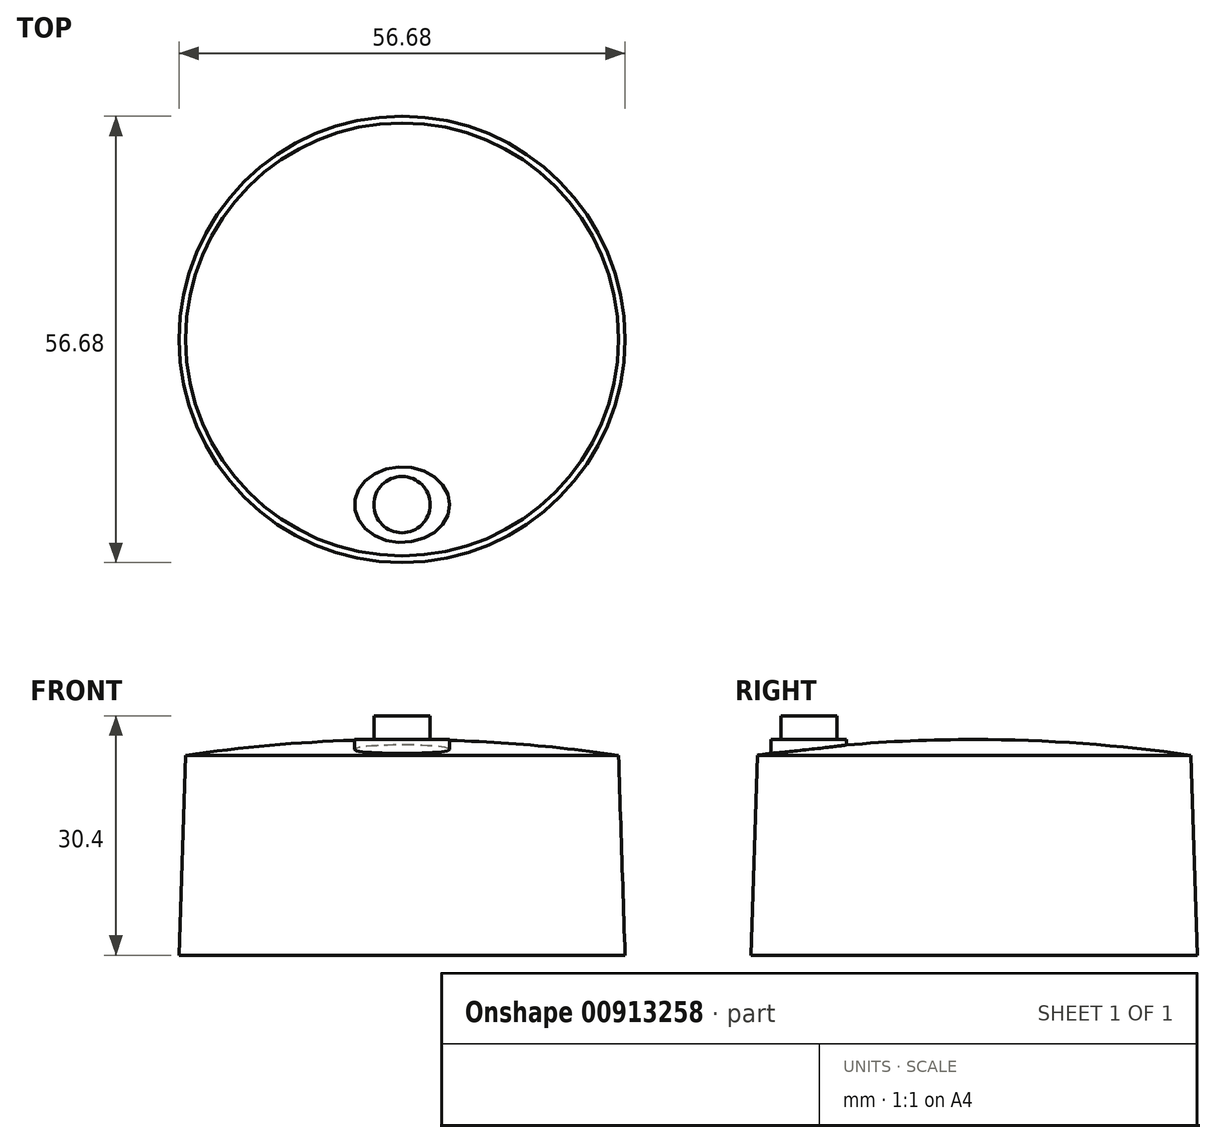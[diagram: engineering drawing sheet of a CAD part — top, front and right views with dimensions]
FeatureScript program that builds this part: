
annotation { "Feature Type Name" : "Feature", "Feature Type Description" : "" }
export const myFeature = defineFeature(function(context is Context, id is Id, definition is map)
    precondition{}
    {
        {
            var Q0;
            Q0=qCreatedBy(makeId("Top.planeOp"),FACE);
            var sketch = newSketch(context, id + "F0", { "sketchPlane" : qUnion([Q0])});
            skCircle(sketch, "E0", {"center": v(0, 0) * mm, "radius": 28.34 * mm});
            skSolve(sketch);
        }
        {
            var Q0;
            Q0=qCreatedBy(makeId("Top.planeOp"),FACE);
            cPlane(context, id + "F1", {"entities" : qUnion([Q0]), "cplaneType" : CPlaneType.OFFSET, "offset" : 25.4 * mm, "width" : 150 * mm, "height" : 150 * mm});
        }
        {
            var Q0;
            Q0=qCreatedBy(id+"F1.planeOp",FACE);
            var sketch = newSketch(context, id + "F2", { "sketchPlane" : qUnion([Q0])});
            skCircle(sketch, "E1", {"center": v(0, 0) * mm, "radius": 27.5 * mm});
            skSolve(sketch);
        }
        {
            var Q0;
            Q0=makeQuery(id+"F0.imprint","IMPRINT",FACE,{"disambiguationData":[TD([[makeQuery(id+"F0.imprint","IMPRINT",EDGE,{"derivedFrom":sQuery(id+"F0.wireOp",EDGE,"E0")}),1.0]])]});
            var Q1;
            Q1=makeQuery(id+"F2.imprint","IMPRINT",FACE,{"disambiguationData":[TD([[makeQuery(id+"F2.imprint","IMPRINT",EDGE,{"derivedFrom":sQuery(id+"F2.wireOp",EDGE,"E1")}),1.0]])]});
            loft(context, id + "F3", {"sheetProfilesArray" : [{ "sheetProfileEntities" : qUnion([Q0]) }, { "sheetProfileEntities" : qUnion([Q1]) }]});
        }
        {
            var Q0;
            Q0=qCreatedBy(makeId("Front.planeOp"),FACE);
            var sketch = newSketch(context, id + "F4", { "sketchPlane" : qUnion([Q0])});
            skArc(sketch, "E2", {"start": v(27.5, 25.4) * mm, "mid": v(13.79, 26.9) * mm, "end": v(0, 27.4) * mm});
            skLineSegment(sketch, "E3", {"start": v(-71.45, 27.4) * mm, "end": v(24.54, 27.4) * mm, "construction": true});
            skLineSegment(sketch, "E4", {"start": v(0, 25.4) * mm, "end": v(27.5, 25.4) * mm});
            skLineSegment(sketch, "E5", {"start": v(0, 27.4) * mm, "end": v(0, 25.4) * mm});
            skSolve(sketch);
        }
        {
            var Q0;
            Q0=makeQuery(id+"F4.imprint","IMPRINT",FACE,{"disambiguationData":[TD([[makeQuery(id+"F4.imprint","IMPRINT",EDGE,{"derivedFrom":sQuery(id+"F4.wireOp",EDGE,"E2")}),1.0]])]});
            var Q1;
            Q1=sQuery(id+"F4.wireOp",EDGE,"E5");
            revolve(context, id + "F5", {"operationType" : NewBodyOperationType.ADD, "surfaceOperationType" : NewSurfaceOperationType.NEW, "entities" : qUnion([Q0]), "axis" : qUnion([Q1]), "revolveType" : RevolveType.FULL});
        }
        {
            var Q0;
            Q0=qCreatedBy(id+"F1.planeOp",FACE);
            var sketch = newSketch(context, id + "F6", { "sketchPlane" : qUnion([Q0])});
            skEllipse(sketch, "E6", {"center": v(0, -21) * mm, "majorRadius": 6.05 * mm, "minorRadius": 4.8 * mm, "majorAxis": v(1, 0)});
            skLineSegment(sketch, "E7.bottom", {"start": v(-6.05, -16.2) * mm, "end": v(6.05, -16.2) * mm, "construction": true});
            skLineSegment(sketch, "E7.top", {"start": v(-6.05, -25.8) * mm, "end": v(6.05, -25.8) * mm, "construction": true});
            skLineSegment(sketch, "E7.left", {"start": v(-6.05, -16.2) * mm, "end": v(-6.05, -25.8) * mm, "construction": true});
            skLineSegment(sketch, "E7.right", {"start": v(6.05, -16.2) * mm, "end": v(6.05, -25.8) * mm, "construction": true});
            skLineSegment(sketch, "E8", {"start": v(0, 0) * mm, "end": v(0, -21) * mm, "construction": true});
            skPoint(sketch, "E9", {"position": v(0, -16.2) * mm});
            skPoint(sketch, "E10", {"position": v(6.05, -21) * mm});
            skLineSegment(sketch, "E11", {"start": v(0, -21) * mm, "end": v(6.05, -21) * mm, "construction": true});
            skLineSegment(sketch, "E12", {"start": v(-34.02, -27.5) * mm, "end": v(34.2, -27.5) * mm, "construction": true});
            skSolve(sketch);
        }
        {
            var Q0;
            Q0=qCreatedBy(id+"F1.planeOp",FACE);
            cPlane(context, id + "F7", {"entities" : qUnion([Q0]), "cplaneType" : CPlaneType.OFFSET, "offset" : 2 * mm, "width" : 150 * mm, "height" : 150 * mm});
        }
        {
            var Q0;
            Q0 = qSketchRegion(id + "F6", true);
            var Q1;
            Q1=qCreatedBy(id+"F7.planeOp",FACE);
            extrude(context, id + "F8", {"entities" : qUnion([Q0]), "operationType" : NewBodyOperationType.ADD, "endBound" : BoundingType.UP_TO_SURFACE, "depth" : 25 * mm, "endBoundEntityFace" : qUnion([Q1]), "offsetDistance" : 25 * mm});
        }
        {
            var Q0;
            Q0=makeQuery(id+"F8.opExtrude","CAP_FACE",FACE,{"disambiguationData":[OSD([sQuery(id+"F6.wireOp",EDGE,"E6")])],"isStart":false});
            var sketch = newSketch(context, id + "F9", { "sketchPlane" : qUnion([Q0])});
            skCircle(sketch, "E13", {"center": v(0, -21) * mm, "radius": 3.58 * mm});
            skSolve(sketch);
        }
        {
            var Q0;
            Q0 = qSketchRegion(id + "F9", true);
            extrude(context, id + "F10", {"entities" : qUnion([Q0]), "operationType" : NewBodyOperationType.ADD, "depth" : 3 * mm, "offsetDistance" : 25 * mm});
        }
    });
